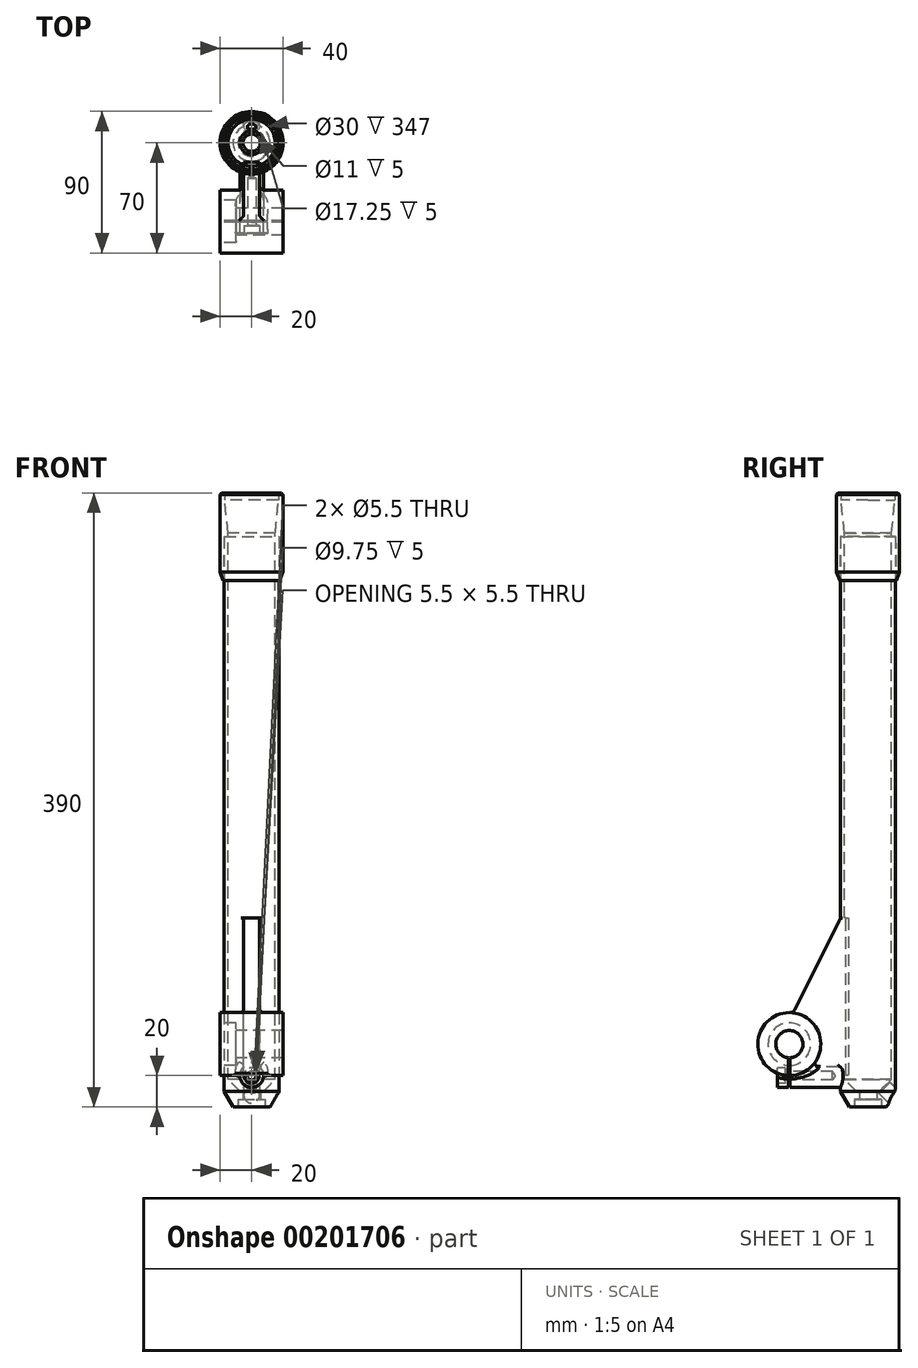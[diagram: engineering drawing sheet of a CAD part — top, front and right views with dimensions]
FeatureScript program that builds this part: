
annotation { "Feature Type Name" : "Feature", "Feature Type Description" : "" }
export const myFeature = defineFeature(function(context is Context, id is Id, definition is map)
    precondition{}
    {
        {
            var Q0;
            Q0=qCreatedBy(makeId("Top.planeOp"),FACE);
            var sketch = newSketch(context, id + "F0", { "sketchPlane" : qUnion([Q0])});
            skCircle(sketch, "E0", {"center": v(0, 0) * mm, "radius": 17.5 * mm});
            skSolve(sketch);
        }
        {
            var Q0;
            Q0=makeQuery(id+"F0.imprint","IMPRINT",FACE,{"disambiguationData":[TD([[makeQuery(id+"F0.imprint","IMPRINT",EDGE,{"derivedFrom":sQuery(id+"F0.wireOp",EDGE,"E0")}),1.0]])]});
            extrude(context, id + "F1", {"entities" : qUnion([Q0]), "depth" : 390 * mm});
        }
        {
            var Q0;
            Q0=qCreatedBy(makeId("Right.planeOp"),FACE);
            var sketch = newSketch(context, id + "F2", { "sketchPlane" : qUnion([Q0])});
            skLineSegment(sketch, "E1", {"start": v(0, 0) * mm, "end": v(0, 571.67) * mm, "construction": true});
            skLineSegment(sketch, "E2.0", {"start": v(-17.5, 390) * mm, "end": v(17.5, 390) * mm});
            skLineSegment(sketch, "E3", {"start": v(0, 390) * mm, "end": v(-15.5, 390) * mm});
            skLineSegment(sketch, "E4", {"start": v(0, 390) * mm, "end": v(0, 10) * mm});
            skLineSegment(sketch, "E5", {"start": v(0, 10) * mm, "end": v(-7.5, 10) * mm});
            skLineSegment(sketch, "E6", {"start": v(-15, 17.5) * mm, "end": v(-15, 364.5) * mm});
            skLineSegment(sketch, "E7", {"start": v(-15, 364.5) * mm, "end": v(-15, 364.5) * mm});
            skLineSegment(sketch, "E8", {"start": v(-7.5, 10) * mm, "end": v(-15, 17.5) * mm});
            skPoint(sketch, "E9.orphan", {"position": v(-15, 10) * mm});
            skLineSegment(sketch, "E10", {"start": v(-15, 364.5) * mm, "end": v(-17.5, 390) * mm});
            skSolve(sketch);
        }
        {
            var Q0;
            Q0=qSketchRegion(id+"F2",true);
            var Q1;
            Q1=sQuery(id+"F2.wireOp",EDGE,"E1");
            revolve(context, id + "F3", {"operationType" : NewBodyOperationType.REMOVE, "entities" : qUnion([Q0]), "axis" : qUnion([Q1]), "revolveType" : RevolveType.FULL, "oppositeDirection" : true});
        }
        {
            var Q0;
            Q0=makeQuery(id+"F1.opExtrude","CAP_FACE",FACE,{"disambiguationData":[OSD([sQuery(id+"F0.wireOp",EDGE,"E0")])],"isStart":true});
            var sketch = newSketch(context, id + "F4", { "sketchPlane" : qUnion([Q0])});
            skPoint(sketch, "E11", {"position": v(0, 0) * mm});
            skSolve(sketch);
        }
        {
            var Q0;
            Q0=sQuery(id+"F4.wireOp",VERTEX,"E11");
            var Q1;
            Q1=makeQuery(id+"F1.opExtrude","SWEPT_BODY",BODY,{"disambiguationData":[OSD([sQuery(id+"F0.wireOp",EDGE,"E0")])]});
            hole(context, id + "F5", {"style" : HoleStyle.C_BORE, "endStyle" : HoleEndStyle.THROUGH, "holeDiameter" : 11 * mm, "cBoreDiameter" : 17.25 * mm, "cBoreDepth" : 5 * mm, "locations" : qUnion([Q0]), "scope" : qUnion([Q1]), "isTappedThrough" : true});
        }
        {
            var Q0;
            Q0=qCreatedBy(makeId("Front.planeOp"),FACE);
            var sketch = newSketch(context, id + "F6", { "sketchPlane" : qUnion([Q0])});
            skLineSegment(sketch, "E12.0", {"start": v(-17, 390) * mm, "end": v(17, 389.39) * mm, "construction": true});
            skLineSegment(sketch, "E13", {"start": v(-17, 390) * mm, "end": v(-20, 390) * mm});
            skLineSegment(sketch, "E14", {"start": v(-20, 390) * mm, "end": v(-20, 340) * mm});
            skLineSegment(sketch, "E15", {"start": v(-17, 390) * mm, "end": v(-18, 334.5) * mm});
            skLineSegment(sketch, "E16", {"start": v(-18, 334.5) * mm, "end": v(-20, 340) * mm});
            skLineSegment(sketch, "E17", {"start": v(0, 515.52) * mm, "end": v(0, 389.7) * mm, "construction": true});
            skPoint(sketch, "E17.endSnap0", {"position": v(0, 389.7) * mm});
            skSolve(sketch);
        }
        {
            var Q0;
            Q0=makeQuery(id+"F6.imprint","IMPRINT",FACE,{"disambiguationData":[TD([[makeQuery(id+"F6.imprint","IMPRINT",EDGE,{"derivedFrom":sQuery(id+"F6.wireOp",EDGE,"E13")}),1.0]])]});
            var Q1;
            Q1=sQuery(id+"F6.wireOp",EDGE,"E17");
            revolve(context, id + "F7", {"operationType" : NewBodyOperationType.ADD, "entities" : qUnion([Q0]), "axis" : qUnion([Q1]), "revolveType" : RevolveType.FULL});
        }
        {
            var Q0;
            Q0=makeQuery(id+"F1.opExtrude","CAP_EDGE",EDGE,{"disambiguationData":[OSD([sQuery(id+"F0.wireOp",EDGE,"E0")])],"isStart":true});
            chamfer(context, id + "F8", {"entities" : qUnion([Q0]), "chamferType" : ChamferType.OFFSET_ANGLE, "width" : 10 * mm, "oppositeDirection" : false, "angle" : 30 * degree, "tangentPropagation" : true});
        }
        {
            var Q0;
            Q0=qCreatedBy(makeId("Right.planeOp"),FACE);
            var sketch = newSketch(context, id + "F9", { "sketchPlane" : qUnion([Q0])});
            skLineSegment(sketch, "E18.0", {"start": v(-17.5, 10) * mm, "end": v(17.5, 10) * mm});
            skPoint(sketch, "E19.0", {"position": v(0, 0) * mm});
            skLineSegment(sketch, "E20", {"start": v(0, 0) * mm, "end": v(0, 120.7) * mm, "construction": true});
            skLineSegment(sketch, "E21", {"start": v(-17.5, 10) * mm, "end": v(-17.5, 153.8) * mm, "construction": true});
            skLineSegment(sketch, "E22", {"start": v(-17.5, 40) * mm, "end": v(-57.5, 40) * mm});
            skLineSegment(sketch, "E23", {"start": v(-57.5, 40) * mm, "end": v(-17.5, 120) * mm});
            skLineSegment(sketch, "E24", {"start": v(-17.5, 120) * mm, "end": v(-17.5, 40) * mm});
            skLineSegment(sketch, "E25.top", {"start": v(-17.5, 20) * mm, "end": v(-57.5, 20) * mm});
            skLineSegment(sketch, "E25.left", {"start": v(-17.5, 40) * mm, "end": v(-17.5, 20) * mm});
            skLineSegment(sketch, "E25.right", {"start": v(-57.5, 40) * mm, "end": v(-57.5, 20) * mm});
            skLineSegment(sketch, "E26.bottom", {"start": v(-17.5, 120) * mm, "end": v(-12.46, 120) * mm});
            skLineSegment(sketch, "E26.top", {"start": v(-17.5, 20) * mm, "end": v(-12.46, 20) * mm});
            skLineSegment(sketch, "E26.left", {"start": v(-17.5, 120) * mm, "end": v(-17.5, 20) * mm});
            skLineSegment(sketch, "E26.right", {"start": v(-12.46, 120) * mm, "end": v(-12.46, 20) * mm});
            skSolve(sketch);
        }
        {
            var Q0;
            Q0=makeQuery(id+"F9.imprint","IMPRINT",FACE,{"disambiguationData":[TD([[makeQuery(id+"F9.imprint","IMPRINT",EDGE,{"derivedFrom":sQuery(id+"F9.wireOp",EDGE,"E23")}),-1.0]])]});
            var Q1;
            Q1=makeQuery(id+"F9.imprint","IMPRINT",FACE,{"disambiguationData":[TD([[makeQuery(id+"F9.imprint","IMPRINT",EDGE,{"derivedFrom":sQuery(id+"F9.wireOp",EDGE,"E22")}),1.0]])]});
            var Q2;
            {var subQ3=sQuery(id+"F9.wireOp",EDGE,"E26.bottom");Q2=makeQuery(id+"F9.imprint","IMPRINT",FACE,{"disambiguationData":[TD([[makeQuery(id+"F9.imprint","IMPRINT",EDGE,{"derivedFrom":subQ3}),-1.0]])]});}
            extrude(context, id + "F10", {"entities" : qUnion([Q0, Q1, Q2]), "operationType" : NewBodyOperationType.ADD, "endBound" : BoundingType.SYMMETRIC, "depth" : 10 * mm});
        }
        {
            var Q0;
            Q0=qCreatedBy(makeId("Right.planeOp"),FACE);
            var sketch = newSketch(context, id + "F11", { "sketchPlane" : qUnion([Q0])});
            skLineSegment(sketch, "E27.0", {"start": v(-57.5, 40) * mm, "end": v(-57.5, 20) * mm});
            skPoint(sketch, "E28.0", {"position": v(0, 0) * mm});
            skCircle(sketch, "E29", {"center": v(-50, 40) * mm, "radius": 20 * mm});
            skSolve(sketch);
        }
        {
            var Q0;
            Q0=makeQuery(id+"F11.imprint","IMPRINT",FACE,{"disambiguationData":[TD([[makeQuery(id+"F11.imprint","IMPRINT",EDGE,{"derivedFrom":sQuery(id+"F11.wireOp",EDGE,"E29")}),1.0]])]});
            extrude(context, id + "F12", {"entities" : qUnion([Q0]), "operationType" : NewBodyOperationType.ADD, "endBound" : BoundingType.SYMMETRIC, "depth" : 40 * mm});
        }
        {
            var Q0;
            Q0=makeQuery(id+"F12.opExtrude","CAP_FACE",FACE,{"disambiguationData":[OSD([sQuery(id+"F11.wireOp",EDGE,"E29")])],"isStart":true});
            var sketch = newSketch(context, id + "F13", { "sketchPlane" : qUnion([Q0])});
            skPoint(sketch, "E30", {"position": v(50, 40) * mm});
            skSolve(sketch);
        }
        {
            var Q0;
            Q0=sQuery(id+"F13.wireOp",VERTEX,"E30");
            var Q1;
            Q1=makeQuery(id+"F1.opExtrude","SWEPT_BODY",BODY,{"disambiguationData":[OSD([sQuery(id+"F0.wireOp",EDGE,"E0")])]});
            hole(context, id + "F14", {"style" : HoleStyle.C_BORE, "endStyle" : HoleEndStyle.THROUGH, "holeDiameter" : 17.24 * mm, "cBoreDiameter" : 27 * mm, "cBoreDepth" : 10 * mm, "locations" : qUnion([Q0]), "scope" : qUnion([Q1]), "isTappedThrough" : true});
        }
        {
            var Q0;
            Q0=makeQuery(id+"F10.opExtrude","SWEPT_FACE",FACE,{"disambiguationData":[OSD([sQuery(id+"F9.wireOp",EDGE,"E25.right")])]});
            var sketch = newSketch(context, id + "F15", { "sketchPlane" : qUnion([Q0])});
            skCircle(sketch, "E31", {"center": v(0, 20) * mm, "radius": 7.5 * mm});
            skSolve(sketch);
        }
        {
            var Q0;
            {var subQ1=sQuery(id+"F9.wireOp",EDGE,"E25.right");var subQ6=makeQuery(id+"F10.opExtrude","SWEPT_EDGE",EDGE,{"disambiguationData":[OSD([sQuery(id+"F9.wireOp",EDGE,"E25.top"),subQ1])]});Q0=makeQuery(id+"F15.imprint","IMPRINT",FACE,{"disambiguationData":[TD([[makeQuery(id+"F15.imprint","IMPRINT",EDGE,{"derivedFrom":subQ6}),1.0]])]});}
            var Q1;
            {var subQ1=sQuery(id+"F9.wireOp",EDGE,"E25.right");var subQ6=makeQuery(id+"F10.opExtrude","SWEPT_EDGE",EDGE,{"disambiguationData":[OSD([sQuery(id+"F9.wireOp",EDGE,"E25.top"),subQ1])]});Q1=makeQuery(id+"F15.imprint","IMPRINT",FACE,{"disambiguationData":[TD([[makeQuery(id+"F15.imprint","IMPRINT",EDGE,{"derivedFrom":subQ6}),-1.0]])]});}
            var Q2;
            Q2=makeQuery(id+"F1.opExtrude","SWEPT_FACE",FACE,{"disambiguationData":[OSD([sQuery(id+"F0.wireOp",EDGE,"E0")])]});
            extrude(context, id + "F16", {"entities" : qUnion([Q0, Q1]), "operationType" : NewBodyOperationType.ADD, "endBound" : BoundingType.UP_TO_SURFACE, "oppositeDirection" : true, "endBoundEntityFace" : qUnion([Q2]), "depth" : 25 * mm});
        }
        {
            var Q0;
            Q0=makeQuery(id+"F16.boolean.opBoolean","MERGE",FACE,{"derivedFrom":[makeQuery(id+"F10.opExtrude","SWEPT_FACE",FACE,{"disambiguationData":[OSD([sQuery(id+"F9.wireOp",EDGE,"E25.right")])]}),makeQuery(id+"F16.opExtrude","CAP_FACE",FACE,{"disambiguationData":[OSD([sQuery(id+"F15.wireOp",EDGE,"E31")])],"isStart":true})]});
            var sketch = newSketch(context, id + "F17", { "sketchPlane" : qUnion([Q0])});
            skPoint(sketch, "E32", {"position": v(0, 20) * mm});
            skSolve(sketch);
        }
        {
            var Q0;
            Q0=sQuery(id+"F17.wireOp",VERTEX,"E32");
            var Q1;
            Q1=makeQuery(id+"F1.opExtrude","SWEPT_BODY",BODY,{"disambiguationData":[OSD([sQuery(id+"F0.wireOp",EDGE,"E0")])]});
            hole(context, id + "F18", {"style" : HoleStyle.C_BORE, "endStyle" : HoleEndStyle.BLIND, "standardTappedOrClearance" : lookupTablePath({ "standard" : "ISO", "fit" : "Normal", "size" : "M5", "type" : "Clearance" }), "standardBlindInLast" : lookupTablePath({ "fit" : "Standard", "standard" : "ISO", "size" : "M5", "type" : "Clearance" }), "holeDiameter" : 5.5 * mm, "cBoreDiameter" : 9.75 * mm, "cBoreDepth" : 5 * mm, "holeDepth" : 35 * mm, "locations" : qUnion([Q0]), "scope" : qUnion([Q1])});
        }
        {
            var Q0;
            Q0=qCreatedBy(makeId("Right.planeOp"),FACE);
            var sketch = newSketch(context, id + "F19", { "sketchPlane" : qUnion([Q0])});
            skCircle(sketch, "E33.0", {"center": v(-50, 40) * mm, "radius": 8.62 * mm, "construction": true});
            skLineSegment(sketch, "E34", {"start": v(-28, 12.5) * mm, "end": v(-68, 12.5) * mm});
            skLineSegment(sketch, "E35", {"start": v(-50, 40) * mm, "end": v(-50, -3.23) * mm, "construction": true});
            skLineSegment(sketch, "E36.bottom", {"start": v(-50.5, 33.24) * mm, "end": v(-49.5, 33.24) * mm});
            skLineSegment(sketch, "E36.top", {"start": v(-50.5, 3.53) * mm, "end": v(-49.5, 3.53) * mm});
            skLineSegment(sketch, "E36.left", {"start": v(-50.5, 33.24) * mm, "end": v(-50.5, 3.53) * mm});
            skLineSegment(sketch, "E36.right", {"start": v(-49.5, 33.24) * mm, "end": v(-49.5, 3.53) * mm});
            skPoint(sketch, "E36.middle", {"position": v(-50, 18.38) * mm});
            skSolve(sketch);
        }
        {
            var Q0;
            {var subQ5=sQuery(id+"F19.wireOp",EDGE,"E36.top");Q0=makeQuery(id+"F19.imprint","IMPRINT",FACE,{"disambiguationData":[TD([[makeQuery(id+"F19.imprint","IMPRINT",EDGE,{"derivedFrom":subQ5}),1.0]])]});}
            var Q1;
            {var subQ5=sQuery(id+"F19.wireOp",EDGE,"E36.bottom");Q1=makeQuery(id+"F19.imprint","IMPRINT",FACE,{"disambiguationData":[TD([[makeQuery(id+"F19.imprint","IMPRINT",EDGE,{"derivedFrom":subQ5}),-1.0]])]});}
            extrude(context, id + "F20", {"entities" : qUnion([Q0, Q1]), "operationType" : NewBodyOperationType.REMOVE, "endBound" : BoundingType.SYMMETRIC, "depth" : 50 * mm});
        }
        {
            var Q0;
            Q0=makeQuery(id+"F10.boolean.opBoolean","INTERSECT",EDGE,{"derivedFrom":[makeQuery(id+"F1.opExtrude","SWEPT_FACE",FACE,{"disambiguationData":[OSD([sQuery(id+"F0.wireOp",EDGE,"E0")])]}),makeQuery(id+"F10.opExtrude","CAP_FACE",FACE,{"disambiguationData":[OSD([sQuery(id+"F9.wireOp",EDGE,"E23"),sQuery(id+"F9.wireOp",EDGE,"E25.top"),sQuery(id+"F9.wireOp",EDGE,"E25.right"),sQuery(id+"F9.wireOp",EDGE,"E26.bottom"),sQuery(id+"F9.wireOp",EDGE,"E26.top"),sQuery(id+"F9.wireOp",EDGE,"E26.right")])],"isStart":false})]});
            var Q1;
            {var subQ0=sQuery(id+"F15.wireOp",EDGE,"E31");var subQ1=sQuery(id+"F9.wireOp",EDGE,"E25.right");var subQ2=makeQuery(id+"F15.imprint","INTERSECT",VERTEX,{"derivedFrom":[makeQuery(id+"F10.opExtrude","CAP_EDGE",EDGE,{"disambiguationData":[OSD([subQ1])],"isStart":true}),subQ0]});Q1=makeQuery(id+"F16.opExtrude","TWEAK_EDGE",EDGE,{"derivedFrom":[makeQuery(id+"F1.opExtrude","SWEPT_FACE",FACE,{"disambiguationData":[OSD([sQuery(id+"F0.wireOp",EDGE,"E0")])]}),makeQuery(id+"F15.imprint","IMPRINT",EDGE,{"disambiguationData":[TD([[subQ2,1.0]])],"derivedFrom":subQ0}),makeQuery(id+"F15.imprint","IMPRINT",EDGE,{"disambiguationData":[TD([[subQ2,-1.0]])],"derivedFrom":subQ0})]});}
            var Q2;
            Q2=makeQuery(id+"F10.boolean.opBoolean","INTERSECT",EDGE,{"derivedFrom":[makeQuery(id+"F1.opExtrude","SWEPT_FACE",FACE,{"disambiguationData":[OSD([sQuery(id+"F0.wireOp",EDGE,"E0")])]}),makeQuery(id+"F10.opExtrude","CAP_FACE",FACE,{"disambiguationData":[OSD([sQuery(id+"F9.wireOp",EDGE,"E23"),sQuery(id+"F9.wireOp",EDGE,"E25.top"),sQuery(id+"F9.wireOp",EDGE,"E25.right"),sQuery(id+"F9.wireOp",EDGE,"E26.bottom"),sQuery(id+"F9.wireOp",EDGE,"E26.top"),sQuery(id+"F9.wireOp",EDGE,"E26.right")])],"isStart":true})]});
            var Q3;
            {var subQ0=sQuery(id+"F9.wireOp",EDGE,"E26.top");var subQ1=sQuery(id+"F9.wireOp",EDGE,"E26.bottom");var subQ2=sQuery(id+"F9.wireOp",EDGE,"E25.top");var subQ3=sQuery(id+"F9.wireOp",EDGE,"E23");var subQ4=makeQuery(id+"F10.opExtrude","CAP_FACE",FACE,{"disambiguationData":[OSD([subQ3,subQ2,sQuery(id+"F9.wireOp",EDGE,"E25.right"),subQ1,subQ0,sQuery(id+"F9.wireOp",EDGE,"E26.right")])],"isStart":false});Q3=makeQuery(id+"F16.boolean.opBoolean","INTERSECT",EDGE,{"derivedFrom":[makeQuery(id+"F12.boolean.opBoolean","SPLIT",FACE,{"disambiguationData":[TD([makeQuery(id+"F1.opExtrude","SWEPT_FACE",FACE,{"disambiguationData":[OSD([sQuery(id+"F0.wireOp",EDGE,"E0")])]})])],"derivedFrom":subQ4}),makeQuery(id+"F16.opExtrude","SWEPT_FACE",FACE,{"disambiguationData":[OSD([sQuery(id+"F15.wireOp",EDGE,"E31")])]})]});}
            var Q4;
            {var subQ0=makeQuery(id+"F12.opExtrude","SWEPT_FACE",FACE,{"disambiguationData":[OSD([sQuery(id+"F11.wireOp",EDGE,"E29")])]});var subQ1=makeQuery(id+"F16.opExtrude","SWEPT_FACE",FACE,{"disambiguationData":[OSD([sQuery(id+"F15.wireOp",EDGE,"E31")])]});Q4=makeQuery(id+"F20.boolean.opBoolean","SPLIT",EDGE,{"disambiguationData":[TD([makeQuery(id+"F20.opExtrude","SWEPT_FACE",FACE,{"disambiguationData":[OSD([sQuery(id+"F19.wireOp",EDGE,"E36.right")])]})])],"derivedFrom":makeQuery(id+"F16.boolean.opBoolean","INTERSECT",EDGE,{"disambiguationData":[OD(1.0)],"derivedFrom":[subQ0,subQ1]})});}
            var Q5;
            Q5=makeQuery(id+"F12.boolean.opBoolean","INTERSECT",EDGE,{"disambiguationData":[OD(0.0)],"derivedFrom":[makeQuery(id+"F10.opExtrude","CAP_FACE",FACE,{"disambiguationData":[OSD([sQuery(id+"F9.wireOp",EDGE,"E23"),sQuery(id+"F9.wireOp",EDGE,"E25.top"),sQuery(id+"F9.wireOp",EDGE,"E25.right"),sQuery(id+"F9.wireOp",EDGE,"E26.bottom"),sQuery(id+"F9.wireOp",EDGE,"E26.top"),sQuery(id+"F9.wireOp",EDGE,"E26.right")])],"isStart":false}),makeQuery(id+"F12.opExtrude","SWEPT_FACE",FACE,{"disambiguationData":[OSD([sQuery(id+"F11.wireOp",EDGE,"E29")])]})]});
            var Q6;
            Q6=makeQuery(id+"F12.boolean.opBoolean","INTERSECT",EDGE,{"disambiguationData":[OD(0.0)],"derivedFrom":[makeQuery(id+"F10.opExtrude","CAP_FACE",FACE,{"disambiguationData":[OSD([sQuery(id+"F9.wireOp",EDGE,"E23"),sQuery(id+"F9.wireOp",EDGE,"E25.top"),sQuery(id+"F9.wireOp",EDGE,"E25.right"),sQuery(id+"F9.wireOp",EDGE,"E26.bottom"),sQuery(id+"F9.wireOp",EDGE,"E26.top"),sQuery(id+"F9.wireOp",EDGE,"E26.right")])],"isStart":true}),makeQuery(id+"F12.opExtrude","SWEPT_FACE",FACE,{"disambiguationData":[OSD([sQuery(id+"F11.wireOp",EDGE,"E29")])]})]});
            var Q7;
            Q7=makeQuery(id+"F12.boolean.opBoolean","INTERSECT",EDGE,{"derivedFrom":[makeQuery(id+"F10.opExtrude","SWEPT_FACE",FACE,{"disambiguationData":[OSD([sQuery(id+"F9.wireOp",EDGE,"E23")])]}),makeQuery(id+"F12.opExtrude","SWEPT_FACE",FACE,{"disambiguationData":[OSD([sQuery(id+"F11.wireOp",EDGE,"E29")])]})]});
            var Q8;
            {var subQ0=makeQuery(id+"F12.opExtrude","SWEPT_FACE",FACE,{"disambiguationData":[OSD([sQuery(id+"F11.wireOp",EDGE,"E29")])]});var subQ1=makeQuery(id+"F16.opExtrude","SWEPT_FACE",FACE,{"disambiguationData":[OSD([sQuery(id+"F15.wireOp",EDGE,"E31")])]});Q8=makeQuery(id+"F20.boolean.opBoolean","SPLIT",EDGE,{"disambiguationData":[TD([makeQuery(id+"F20.opExtrude","SWEPT_FACE",FACE,{"disambiguationData":[OSD([sQuery(id+"F19.wireOp",EDGE,"E36.right")])]})])],"derivedFrom":makeQuery(id+"F16.boolean.opBoolean","INTERSECT",EDGE,{"disambiguationData":[OD(0.0)],"derivedFrom":[subQ0,subQ1]})});}
            var Q9;
            {var subQ0=makeQuery(id+"F12.opExtrude","SWEPT_FACE",FACE,{"disambiguationData":[OSD([sQuery(id+"F11.wireOp",EDGE,"E29")])]});var subQ1=makeQuery(id+"F16.opExtrude","SWEPT_FACE",FACE,{"disambiguationData":[OSD([sQuery(id+"F15.wireOp",EDGE,"E31")])]});Q9=makeQuery(id+"F20.boolean.opBoolean","SPLIT",EDGE,{"disambiguationData":[TD([makeQuery(id+"F20.opExtrude","SWEPT_FACE",FACE,{"disambiguationData":[OSD([sQuery(id+"F19.wireOp",EDGE,"E36.left")])]})])],"derivedFrom":makeQuery(id+"F16.boolean.opBoolean","INTERSECT",EDGE,{"disambiguationData":[OD(0.0)],"derivedFrom":[subQ0,subQ1]})});}
            var Q10;
            {var subQ0=makeQuery(id+"F12.opExtrude","SWEPT_FACE",FACE,{"disambiguationData":[OSD([sQuery(id+"F11.wireOp",EDGE,"E29")])]});var subQ1=makeQuery(id+"F16.opExtrude","SWEPT_FACE",FACE,{"disambiguationData":[OSD([sQuery(id+"F15.wireOp",EDGE,"E31")])]});Q10=makeQuery(id+"F20.boolean.opBoolean","SPLIT",EDGE,{"disambiguationData":[TD([makeQuery(id+"F20.opExtrude","SWEPT_FACE",FACE,{"disambiguationData":[OSD([sQuery(id+"F19.wireOp",EDGE,"E36.left")])]})])],"derivedFrom":makeQuery(id+"F16.boolean.opBoolean","INTERSECT",EDGE,{"disambiguationData":[OD(1.0)],"derivedFrom":[subQ0,subQ1]})});}
            fillet(context, id + "F21", {"entities" : qUnion([Q0, Q1, Q2, Q3, Q4, Q5, Q6, Q7, Q8, Q9, Q10]), "radius" : 3 * mm, "tangentPropagation" : true, "allowEdgeOverflow" : false});
        }
        {
            var Q0;
            Q0=makeQuery(id+"F5.hole-0.boolean.opBoolean","COPY",EDGE,{"derivedFrom":makeQuery(id+"F5.hole-0.opRevolve","SWEPT_EDGE",EDGE,{"disambiguationData":[OSD([sQuery(id+"F5.hole-0.sketch.wireOp",EDGE,"cbore_start_line_2"),sQuery(id+"F5.hole-0.sketch.wireOp",EDGE,"cbore_start_line_3")])]})});
            var Q1;
            Q1=makeQuery(id+"F7.opRevolve","SWEPT_EDGE",EDGE,{"disambiguationData":[OSD([sQuery(id+"F6.wireOp",EDGE,"E13"),sQuery(id+"F6.wireOp",EDGE,"E14")])]});
            chamfer(context, id + "F22", {"entities" : qUnion([Q0, Q1]), "width" : 1 * mm, "tangentPropagation" : true});
        }
        {
            var Q0;
            Q0=qCreatedBy(makeId("Right.planeOp"),FACE);
            var sketch = newSketch(context, id + "F23", { "sketchPlane" : qUnion([Q0])});
            skLineSegment(sketch, "E37.0", {"start": v(14.19, 0) * mm, "end": v(0, 0) * mm});
            skLineSegment(sketch, "E38", {"start": v(0, 0) * mm, "end": v(14.19, 0) * mm});
            skLineSegment(sketch, "E39", {"start": v(14.19, 0) * mm, "end": v(23.9, 9.71) * mm});
            skSolve(sketch);
        }
        {
            var Q0;
            Q0=sQuery(id+"F23.wireOp",EDGE,"E39");
            cPlane(context, id + "F24", {"entities" : qUnion([Q0]), "cplaneType" : CPlaneType.LINE_ANGLE, "offset" : 25 * mm, "angle" : 0 * degree, "width" : 150 * mm, "height" : 150 * mm});
        }
        {
            var Q0;
            Q0=qCreatedBy(id+"F24.planeOp",FACE);
            var sketch = newSketch(context, id + "F25", { "sketchPlane" : qUnion([Q0])});
            skLineSegment(sketch, "E40.0", {"start": v(0, 10.03) * mm, "end": v(0, 0) * mm});
            skPoint(sketch, "E41", {"position": v(0, 16.03) * mm});
            skSolve(sketch);
        }
        {
            var Q0;
            Q0=sQuery(id+"F25.wireOp",VERTEX,"E41");
            var Q1;
            Q1=makeQuery(id+"F1.opExtrude","SWEPT_BODY",BODY,{"disambiguationData":[OSD([sQuery(id+"F0.wireOp",EDGE,"E0")])]});
            hole(context, id + "F26", {"style" : HoleStyle.C_BORE, "endStyle" : HoleEndStyle.BLIND, "oppositeDirection" : true, "holeDiameter" : 5.5 * mm, "cBoreDiameter" : 10 * mm, "cBoreDepth" : 5 * mm, "holeDepth" : 20 * mm, "locations" : qUnion([Q0]), "scope" : qUnion([Q1])});
        }
    });
